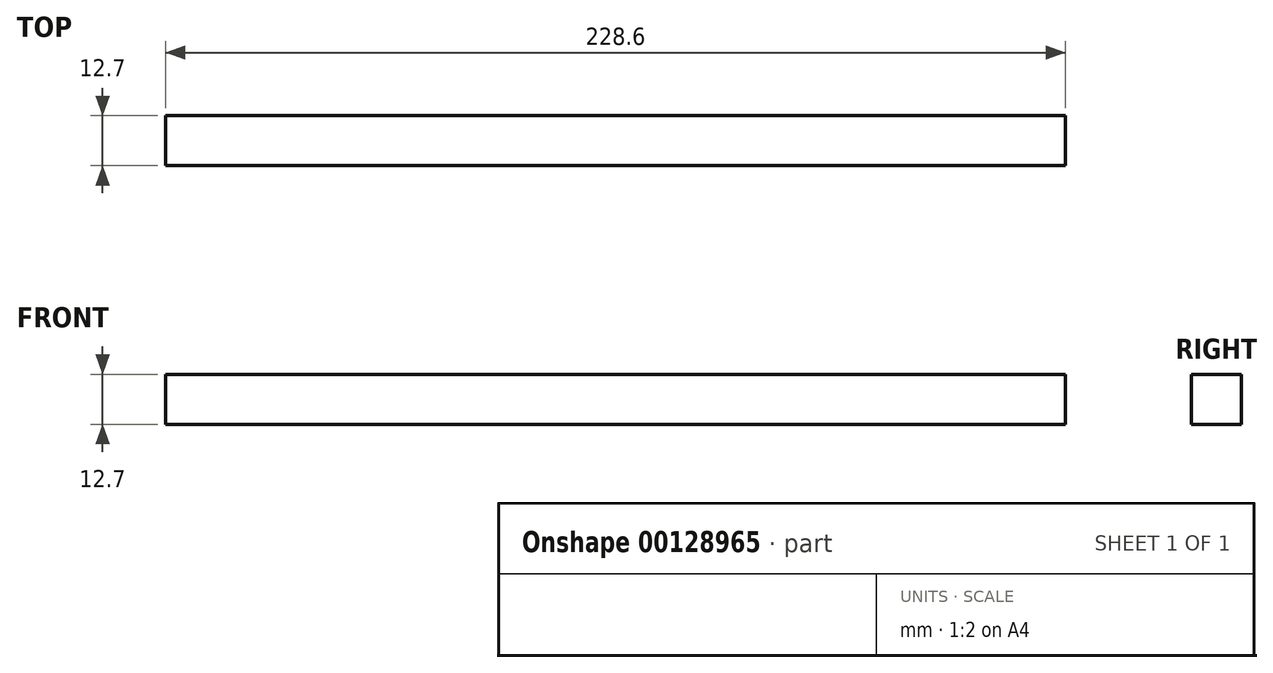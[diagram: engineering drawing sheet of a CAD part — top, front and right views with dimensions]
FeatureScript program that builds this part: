
annotation { "Feature Type Name" : "Feature", "Feature Type Description" : "" }
export const myFeature = defineFeature(function(context is Context, id is Id, definition is map)
    precondition{}
    {
        {
            var Q0;
            Q0=qCreatedBy(makeId("Front.planeOp"),FACE);
            var sketch = newSketch(context, id + "F0", { "sketchPlane" : qUnion([Q0])});
            skLineSegment(sketch, "E0.bottom", {"start": v(0, 0) * mm, "end": v(228.6, 0) * mm});
            skLineSegment(sketch, "E0.top", {"start": v(0, 12.7) * mm, "end": v(228.6, 12.7) * mm});
            skLineSegment(sketch, "E0.left", {"start": v(0, 0) * mm, "end": v(0, 12.7) * mm});
            skLineSegment(sketch, "E0.right", {"start": v(228.6, 0) * mm, "end": v(228.6, 12.7) * mm});
            skSolve(sketch);
        }
        {
            var Q0;
            Q0 = qSketchRegion(id + "F0", true);
            extrude(context, id + "F1", {"entities" : qUnion([Q0]), "depth" : 12.7 * mm});
        }
    });
